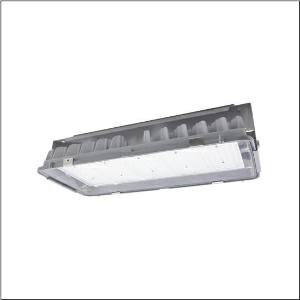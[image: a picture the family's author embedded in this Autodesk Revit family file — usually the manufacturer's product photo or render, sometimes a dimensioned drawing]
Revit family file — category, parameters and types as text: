
# Revit family: highbay_11xtreme_51hf61da4hma
name_source: partatom
category: Lighting Fixtures
units: mm (PartAtom-declared; Revit-internal decimal feet)

## family parameters
Cut with Voids When Loaded = No
Host = Face
Light Source = No
Part Type = Normal
Room Calculation Point = No
Round Connector Dimension = Use Diameter
Shared = No

## types (1)
- --- (1 x LED, 18700 lm, 96.3 W, 4000K)
    Apparent Load = 96 VA
    CIE Flux Codes = 88 96 99 100 100
    Color Rendering = 80
    Color Temperature = 4000K
    Default Elevation = 1800 mm
    Description = Highbay 11Xtreme, LED high bay luminaire, primary light control with lens, of PMMA, primary optical cover: cover, of toughened safety glass, light emission: direct distribution, primary light characteristic: symmetric, installation type: suspended mounting, surface-mounted, 1x LED module,for 1x LED, rated luminous flux: 18.700lm, luminous efficacy: 194lm/W, light colour: 840, colour temperature: 4000K, with cable H07RN-F 5x 1.5mm², mains connection: 220..240V, AC, 50/60Hz, cable length: 1,5m, rated input power: 96W, luminaire housing, of diecast aluminium, coated, silver, length: 595mm, width: 280mm, height: 195mm, protection rating (complete): IP66, insulation class (complete): insulation class I (protective earthing), certification: CE, ENEC, UKCA, protection symbol: D, ball protection: ball impact resistant according to DIN VDE 0710 part 13 (with chain suspension), impact resistance: IK08, permissible operating ambient temperature: -25..+70°C, reducing of maximum allowable ambient temperature of 5°C with ceiling mounting, packaging unit: 1 piece
    Height = 157 mm
    Lamp = 1 x LED
    Lamp Light Flux = 18700 lm
    Lamp Power = 96.3 W
    Lamp count = 1
    Length = 593 mm
    Luminous efficacy = 194 lm/W
    Manufacturer = Siteco
    ModVariant = No
    Model = 51HF61DA4HMA
    Mounting Place = Ceiling
    Mounting Type = Pendant
    Number of Poles = 1
    OnlyDefault = Yes
    Power Factor = 1
    Product Name = Highbay 11Xtreme
    Product group = LED high bay luminaire
    ProductGroupID = 903
    Protection Class = Protection class I
    Protection Degree = IP 66
    RLX_Detail_Level = 1
    RLX_Emergency_Light_Flux = 0 lm
    RLX_Emergency_Type = 0
    RLX_Emergency_Type_DB = No
    RlxData = <blob elided: 27725 chars, md5=4870a767>
    Socket = socket
    Standby Power = 0 W
    System Light Flux = 18700 lm
    System Power = 96 W
    Type Comments = factory setting: luminous flux: 100 % | dim-lin: 254 | 650 mA
    Type Image = l_1258342.jpg
    URL = http://relux.com
    VarID = @adj_052935
    Voltage = 0 V
    Weight = 0.00 kg
    Width = 278 mm

## geometry (parser evidence)
native form markers: Blend x4, Sweep x11
no freeform markers — native parametric forms only
